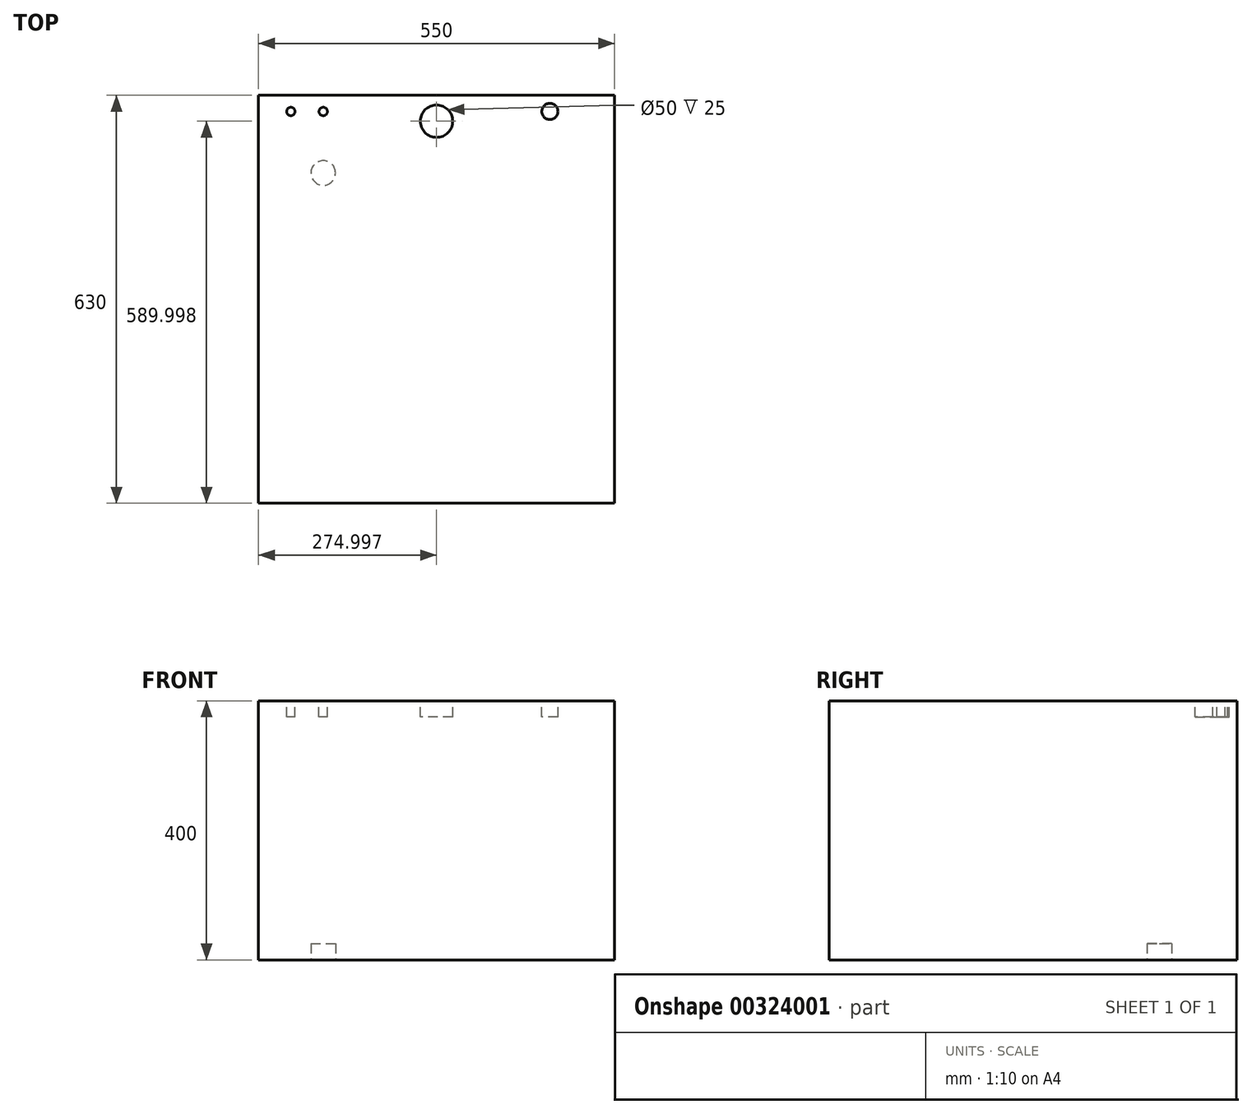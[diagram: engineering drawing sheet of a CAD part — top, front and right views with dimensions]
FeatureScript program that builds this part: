
annotation { "Feature Type Name" : "Feature", "Feature Type Description" : "" }
export const myFeature = defineFeature(function(context is Context, id is Id, definition is map)
    precondition{}
    {
        {
            var Q0;
            Q0=qCreatedBy(makeId("Top.planeOp"),FACE);
            var sketch = newSketch(context, id + "F0", { "sketchPlane" : qUnion([Q0])});
            skLineSegment(sketch, "E0.bottom", {"start": v(-415.33, -13.3) * mm, "end": v(134.67, -13.3) * mm});
            skLineSegment(sketch, "E0.top", {"start": v(-415.33, -643.3) * mm, "end": v(134.67, -643.3) * mm});
            skLineSegment(sketch, "E0.left", {"start": v(-415.33, -13.3) * mm, "end": v(-415.33, -643.3) * mm});
            skLineSegment(sketch, "E0.right", {"start": v(134.67, -13.3) * mm, "end": v(134.67, -643.3) * mm});
            skSolve(sketch);
        }
        {
            var Q0;
            Q0=makeQuery(id+"F0.imprint","IMPRINT",FACE,{"disambiguationData":[TD([[makeQuery(id+"F0.imprint","IMPRINT",EDGE,{"derivedFrom":sQuery(id+"F0.wireOp",EDGE,"E0.bottom")}),-1.0]])]});
            extrude(context, id + "F1", {"entities" : qUnion([Q0]), "oppositeDirection" : true, "depth" : 400 * mm, "offsetDistance" : 25 * mm});
        }
        {
            var Q0;
            Q0=makeQuery(id+"F1.opExtrude","CAP_FACE",FACE,{"disambiguationData":[OSD([sQuery(id+"F0.wireOp",EDGE,"E0.bottom"),sQuery(id+"F0.wireOp",EDGE,"E0.top"),sQuery(id+"F0.wireOp",EDGE,"E0.left"),sQuery(id+"F0.wireOp",EDGE,"E0.right")])],"isStart":false});
            var sketch = newSketch(context, id + "F2", { "sketchPlane" : qUnion([Q0])});
            skCircle(sketch, "E1", {"center": v(-315.33, 133.3) * mm, "radius": 19 * mm});
            skSolve(sketch);
        }
        {
            var Q0;
            Q0 = qSketchRegion(id + "F2", true);
            extrude(context, id + "F3", {"entities" : qUnion([Q0]), "operationType" : NewBodyOperationType.REMOVE, "oppositeDirection" : true, "depth" : 25 * mm});
        }
        {
            var Q0;
            Q0=makeQuery(id+"F1.opExtrude","CAP_FACE",FACE,{"disambiguationData":[OSD([sQuery(id+"F0.wireOp",EDGE,"E0.bottom"),sQuery(id+"F0.wireOp",EDGE,"E0.top"),sQuery(id+"F0.wireOp",EDGE,"E0.left"),sQuery(id+"F0.wireOp",EDGE,"E0.right")])],"isStart":true});
            var sketch = newSketch(context, id + "F4", { "sketchPlane" : qUnion([Q0])});
            skCircle(sketch, "E2", {"center": v(34.67, -38.3) * mm, "radius": 12.5 * mm});
            skCircle(sketch, "E3", {"center": v(-365.33, -38.3) * mm, "radius": 6.5 * mm});
            skCircle(sketch, "E4", {"center": v(-140.33, -53.3) * mm, "radius": 25 * mm});
            skPoint(sketch, "E5", {"position": v(-140.33, -13.3) * mm});
            skCircle(sketch, "E6", {"center": v(-315.33, -38.3) * mm, "radius": 6.5 * mm});
            skSolve(sketch);
        }
        {
            var Q0;
            Q0 = qSketchRegion(id + "F4", true);
            extrude(context, id + "F5", {"entities" : qUnion([Q0]), "operationType" : NewBodyOperationType.REMOVE, "oppositeDirection" : true, "depth" : 25 * mm});
        }
    });
